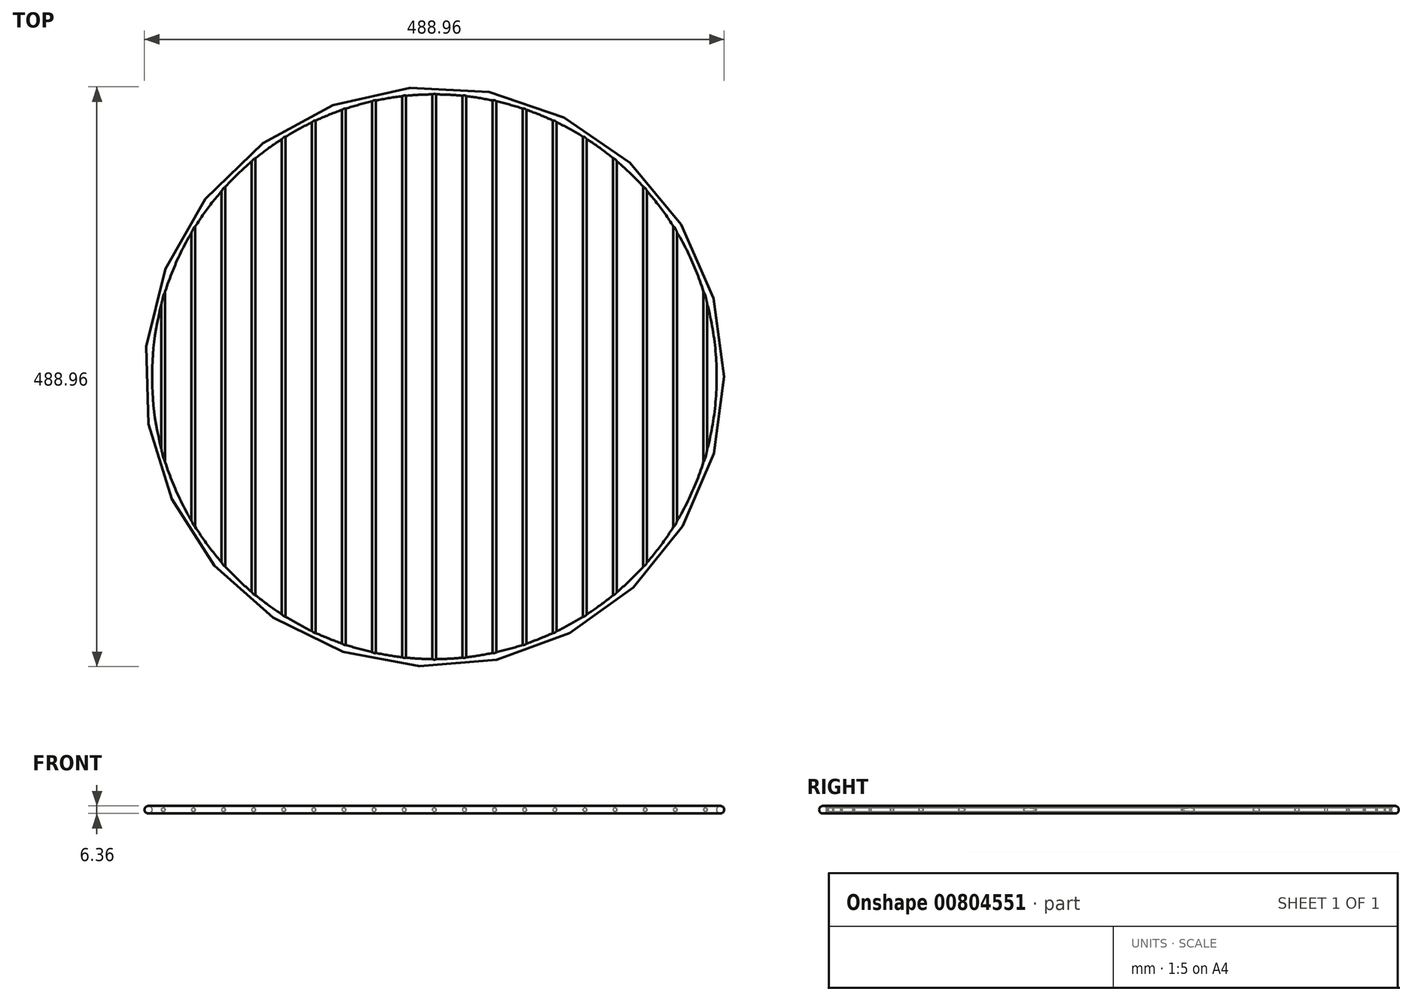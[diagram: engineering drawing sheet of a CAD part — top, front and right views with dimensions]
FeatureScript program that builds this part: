
annotation { "Feature Type Name" : "Feature", "Feature Type Description" : "" }
export const myFeature = defineFeature(function(context is Context, id is Id, definition is map)
    precondition{}
    {
        {
            var Q0;
            Q0=qCreatedBy(makeId("Front.planeOp"),FACE);
            var sketch = newSketch(context, id + "F0", { "sketchPlane" : qUnion([Q0])});
            skCircle(sketch, "E0", {"center": v(241.3, 0) * mm, "radius": 3.18 * mm});
            skLineSegment(sketch, "E1", {"start": v(0, 0) * mm, "end": v(0, 32.12) * mm, "construction": true});
            skSolve(sketch);
        }
        {
            var Q0;
            Q0=makeQuery(id+"F0.imprint","IMPRINT",FACE,{"disambiguationData":[TD([[makeQuery(id+"F0.imprint","IMPRINT",EDGE,{"derivedFrom":sQuery(id+"F0.wireOp",EDGE,"E0")}),1.0]])]});
            var Q1;
            Q1=sQuery(id+"F0.wireOp",EDGE,"E1");
            revolve(context, id + "F1", {"entities" : qUnion([Q0]), "axis" : qUnion([Q1]), "revolveType" : RevolveType.FULL, "surfaceOperationType" : NewSurfaceOperationType.NEW});
        }
        {
            var Q0;
            Q0=qCreatedBy(makeId("Front.planeOp"),FACE);
            var sketch = newSketch(context, id + "F2", { "sketchPlane" : qUnion([Q0])});
            skCircle(sketch, "E2", {"center": v(0, 0) * mm, "radius": 1.59 * mm});
            skCircle(sketch, "E3.1.0.0", {"center": v(25.4, 0) * mm, "radius": 1.59 * mm});
            skCircle(sketch, "E3.2.0.0", {"center": v(50.8, 0) * mm, "radius": 1.59 * mm});
            skCircle(sketch, "E3.3.0.0", {"center": v(76.2, 0) * mm, "radius": 1.59 * mm});
            skCircle(sketch, "E3.4.0.0", {"center": v(101.6, 0) * mm, "radius": 1.59 * mm});
            skCircle(sketch, "E3.5.0.0", {"center": v(127, 0) * mm, "radius": 1.59 * mm});
            skCircle(sketch, "E3.6.0.0", {"center": v(152.4, 0) * mm, "radius": 1.59 * mm});
            skCircle(sketch, "E3.7.0.0", {"center": v(177.8, 0) * mm, "radius": 1.59 * mm});
            skCircle(sketch, "E3.8.0.0", {"center": v(203.2, 0) * mm, "radius": 1.59 * mm});
            skCircle(sketch, "E3.9.0.0", {"center": v(228.6, 0) * mm, "radius": 1.59 * mm});
            skLineSegment(sketch, "E3.direction1", {"start": v(0, 0) * mm, "end": v(25.4, 0) * mm, "construction": true});
            skCircle(sketch, "E4.1.0.0", {"center": v(-25.4, 0) * mm, "radius": 1.59 * mm});
            skCircle(sketch, "E4.2.0.0", {"center": v(-50.8, 0) * mm, "radius": 1.59 * mm});
            skCircle(sketch, "E4.3.0.0", {"center": v(-76.2, 0) * mm, "radius": 1.59 * mm});
            skCircle(sketch, "E4.4.0.0", {"center": v(-101.6, 0) * mm, "radius": 1.59 * mm});
            skCircle(sketch, "E4.5.0.0", {"center": v(-127, 0) * mm, "radius": 1.59 * mm});
            skCircle(sketch, "E4.6.0.0", {"center": v(-152.4, 0) * mm, "radius": 1.59 * mm});
            skCircle(sketch, "E4.7.0.0", {"center": v(-177.8, 0) * mm, "radius": 1.59 * mm});
            skCircle(sketch, "E4.8.0.0", {"center": v(-203.2, 0) * mm, "radius": 1.59 * mm});
            skCircle(sketch, "E4.9.0.0", {"center": v(-228.6, 0) * mm, "radius": 1.59 * mm});
            skLineSegment(sketch, "E4.direction1", {"start": v(0, 0) * mm, "end": v(-25.4, 0) * mm, "construction": true});
            skSolve(sketch);
        }
        {
            var Q0;
            Q0=qSketchRegion(id+"F2",true);
            extrude(context, id + "F3", {"entities" : qUnion([Q0]), "operationType" : NewBodyOperationType.ADD, "endBound" : BoundingType.UP_TO_NEXT, "depth" : 25.4 * mm, "hasSecondDirection" : true, "secondDirectionBound" : BoundingType.UP_TO_NEXT, "secondDirectionOppositeDirection" : true, "secondDirectionDepth" : 25.4 * mm});
        }
    });
